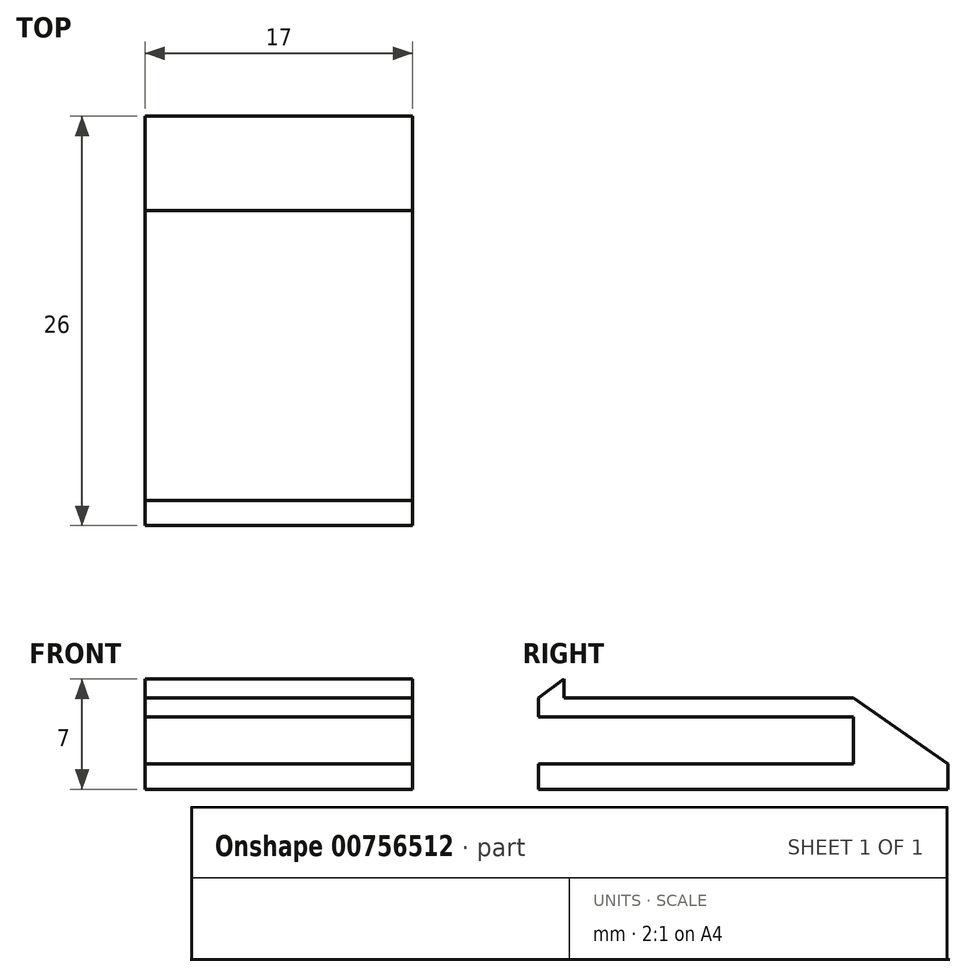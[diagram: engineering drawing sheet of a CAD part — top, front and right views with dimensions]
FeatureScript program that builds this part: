
annotation { "Feature Type Name" : "Feature", "Feature Type Description" : "" }
export const myFeature = defineFeature(function(context is Context, id is Id, definition is map)
    precondition{}
    {
        {
            var Q0;
            Q0=qCreatedBy(makeId("Top.planeOp"),FACE);
            var sketch = newSketch(context, id + "F0", { "sketchPlane" : qUnion([Q0])});
            skLineSegment(sketch, "E0.bottom", {"start": v(8.5, -10) * mm, "end": v(-8.5, -10) * mm});
            skLineSegment(sketch, "E0.top", {"start": v(8.5, 10) * mm, "end": v(-8.5, 10) * mm});
            skLineSegment(sketch, "E0.left", {"start": v(8.5, -10) * mm, "end": v(8.5, 10) * mm});
            skLineSegment(sketch, "E0.right", {"start": v(-8.5, -10) * mm, "end": v(-8.5, 10) * mm});
            skPoint(sketch, "E0.middle", {"position": v(0, 0) * mm});
            skSolve(sketch);
        }
        {
            var Q0;
            Q0 = qSketchRegion(id + "F0", true);
            extrude(context, id + "F1", {"entities" : qUnion([Q0]), "depth" : 1.2 * mm, "offsetDistance" : 25 * mm});
        }
        {
            var Q0;
            Q0=qCreatedBy(makeId("Right.planeOp"),FACE);
            var sketch = newSketch(context, id + "F2", { "sketchPlane" : qUnion([Q0])});
            skLineSegment(sketch, "E1", {"start": v(0, 0) * mm, "end": v(0, 1.2) * mm});
            skLineSegment(sketch, "E2", {"start": v(0, 1.2) * mm, "end": v(-8.4, 1.2) * mm});
            skLineSegment(sketch, "E3", {"start": v(-8.4, 1.2) * mm, "end": v(-8.4, 2.4) * mm});
            skLineSegment(sketch, "E4", {"start": v(-8.4, 1.2) * mm, "end": v(-10, 1.2) * mm});
            skLineSegment(sketch, "E5", {"start": v(-10, 1.2) * mm, "end": v(-8.4, 2.4) * mm});
            skSolve(sketch);
        }
        {
            var Q0;
            Q0 = qSketchRegion(id + "F2", true);
            extrude(context, id + "F3", {"entities" : qUnion([Q0]), "operationType" : NewBodyOperationType.ADD, "endBound" : BoundingType.SYMMETRIC, "depth" : 17 * mm, "offsetDistance" : 25 * mm});
        }
        {
            var Q0;
            Q0=qCreatedBy(makeId("Right.planeOp"),FACE);
            var sketch = newSketch(context, id + "F4", { "sketchPlane" : qUnion([Q0])});
            skLineSegment(sketch, "E6", {"start": v(0, 0) * mm, "end": v(10, 0) * mm});
            skLineSegment(sketch, "E7", {"start": v(10, 0) * mm, "end": v(10, -3) * mm});
            skLineSegment(sketch, "E8", {"start": v(10, 0) * mm, "end": v(10, 1.2) * mm});
            skLineSegment(sketch, "E9", {"start": v(10, 1.2) * mm, "end": v(16, -3) * mm});
            skLineSegment(sketch, "E10", {"start": v(10, -3) * mm, "end": v(-10, -3) * mm});
            skLineSegment(sketch, "E11", {"start": v(-10, -3) * mm, "end": v(-10, -4.6) * mm});
            skLineSegment(sketch, "E12", {"start": v(-10, -4.6) * mm, "end": v(16, -4.6) * mm});
            skLineSegment(sketch, "E13", {"start": v(16, -4.6) * mm, "end": v(16, -3) * mm});
            skSolve(sketch);
        }
        {
            var Q0;
            Q0 = qSketchRegion(id + "F4", true);
            extrude(context, id + "F5", {"entities" : qUnion([Q0]), "operationType" : NewBodyOperationType.ADD, "endBound" : BoundingType.SYMMETRIC, "depth" : 17 * mm, "offsetDistance" : 25 * mm});
        }
    });
